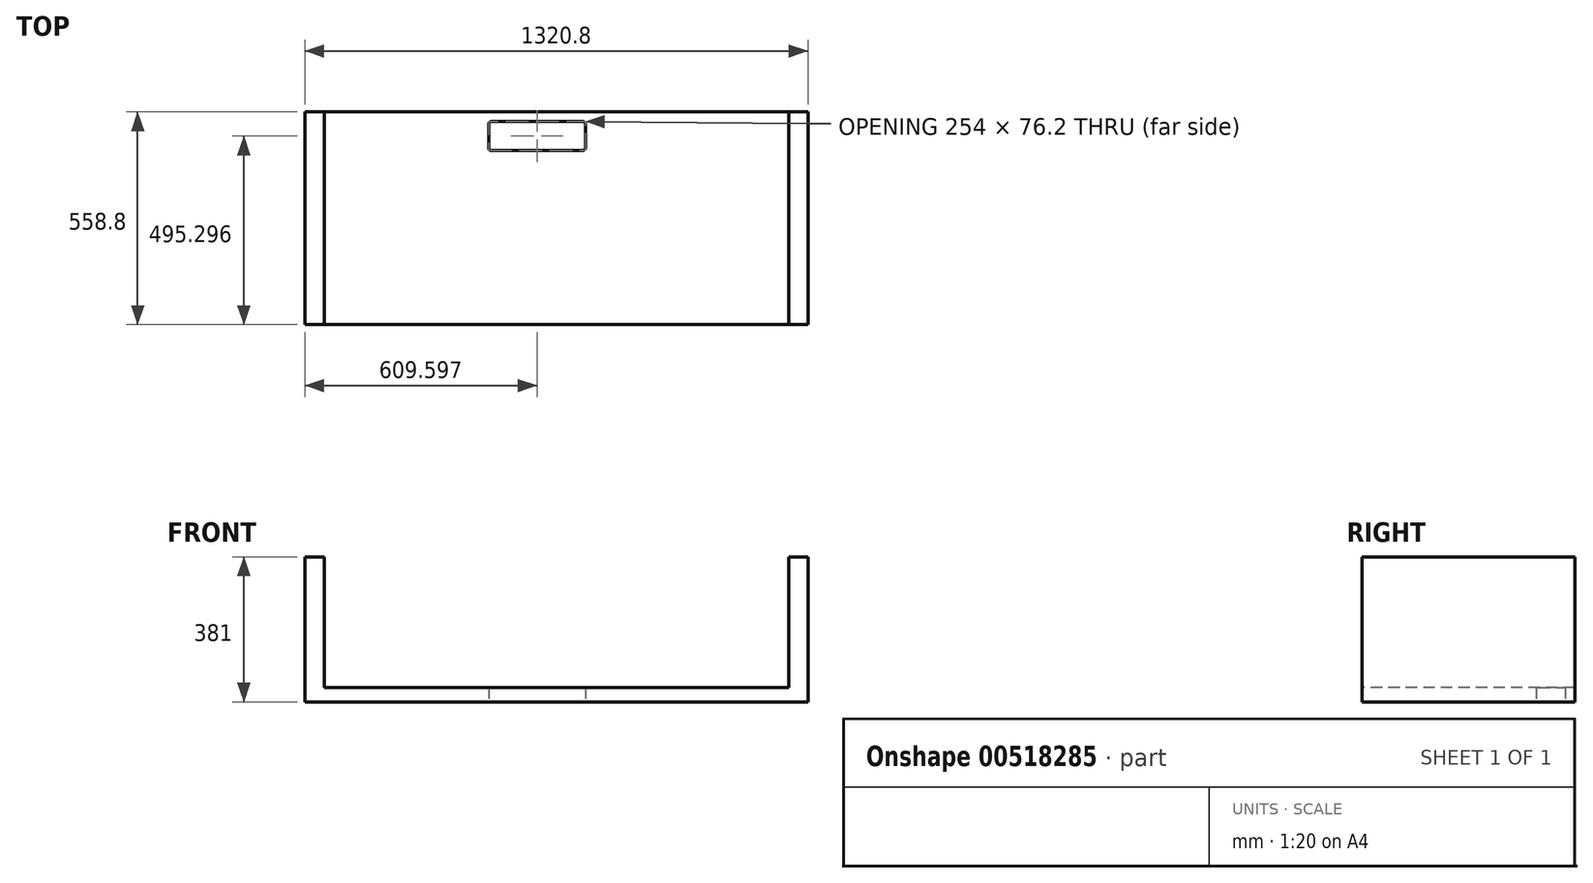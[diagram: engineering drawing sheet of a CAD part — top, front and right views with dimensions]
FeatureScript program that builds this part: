
annotation { "Feature Type Name" : "Feature", "Feature Type Description" : "" }
export const myFeature = defineFeature(function(context is Context, id is Id, definition is map)
    precondition{}
    {
        {
            var Q0;
            Q0=qCreatedBy(makeId("Top.planeOp"),FACE);
            var sketch = newSketch(context, id + "F0", { "sketchPlane" : qUnion([Q0])});
            skLineSegment(sketch, "E0.bottom", {"start": v(-660.38, -103.16) * mm, "end": v(660.42, -103.16) * mm});
            skLineSegment(sketch, "E0.top", {"start": v(-660.38, -661.96) * mm, "end": v(660.42, -661.96) * mm});
            skLineSegment(sketch, "E0.left", {"start": v(-660.38, -103.16) * mm, "end": v(-660.38, -661.96) * mm});
            skLineSegment(sketch, "E0.right", {"start": v(660.42, -103.16) * mm, "end": v(660.42, -661.96) * mm});
            skSolve(sketch);
        }
        {
            var Q0;
            Q0=makeQuery(id+"F0.imprint","IMPRINT",FACE,{"disambiguationData":[TD([[makeQuery(id+"F0.imprint","IMPRINT",EDGE,{"derivedFrom":sQuery(id+"F0.wireOp",EDGE,"E0.bottom")}),-1.0]])]});
            extrude(context, id + "F1", {"entities" : qUnion([Q0]), "depth" : 38.1 * mm, "offsetDistance" : 25.4 * mm});
        }
        {
            var Q0;
            Q0=makeQuery(id+"F1.opExtrude","CAP_FACE",FACE,{"disambiguationData":[OSD([sQuery(id+"F0.wireOp",EDGE,"E0.bottom"),sQuery(id+"F0.wireOp",EDGE,"E0.top"),sQuery(id+"F0.wireOp",EDGE,"E0.left"),sQuery(id+"F0.wireOp",EDGE,"E0.right")])],"isStart":false});
            var sketch = newSketch(context, id + "F2", { "sketchPlane" : qUnion([Q0])});
            skLineSegment(sketch, "E1.bottom", {"start": v(-660.38, -103.16) * mm, "end": v(-609.58, -103.16) * mm});
            skLineSegment(sketch, "E1.top", {"start": v(-660.38, -661.96) * mm, "end": v(-609.58, -661.96) * mm});
            skLineSegment(sketch, "E1.left", {"start": v(-660.38, -103.16) * mm, "end": v(-660.38, -661.96) * mm});
            skLineSegment(sketch, "E1.right", {"start": v(-609.58, -103.16) * mm, "end": v(-609.58, -661.96) * mm});
            skLineSegment(sketch, "E2.bottom", {"start": v(660.42, -103.16) * mm, "end": v(609.62, -103.16) * mm});
            skLineSegment(sketch, "E2.top", {"start": v(660.42, -661.96) * mm, "end": v(609.62, -661.96) * mm});
            skLineSegment(sketch, "E2.left", {"start": v(660.42, -103.16) * mm, "end": v(660.42, -661.96) * mm});
            skLineSegment(sketch, "E2.right", {"start": v(609.62, -103.16) * mm, "end": v(609.62, -661.96) * mm});
            skLineSegment(sketch, "E3.left", {"start": v(-609.58, -300.01) * mm, "end": v(-609.58, -319.06) * mm});
            skLineSegment(sketch, "E3.right", {"start": v(609.62, -300.01) * mm, "end": v(609.62, -319.06) * mm});
            skLineSegment(sketch, "E4.bottom", {"start": v(-177.78, -128.56) * mm, "end": v(76.22, -128.56) * mm});
            skLineSegment(sketch, "E4.top", {"start": v(-177.78, -204.76) * mm, "end": v(76.22, -204.76) * mm});
            skLineSegment(sketch, "E4.left", {"start": v(-177.78, -128.56) * mm, "end": v(-177.78, -204.76) * mm});
            skLineSegment(sketch, "E4.right", {"start": v(76.22, -128.56) * mm, "end": v(76.22, -204.76) * mm});
            skSolve(sketch);
        }
        {
            var Q0;
            Q0=makeQuery(id+"F2.imprint","IMPRINT",FACE,{"disambiguationData":[TD([[makeQuery(id+"F2.imprint","IMPRINT",EDGE,{"derivedFrom":sQuery(id+"F2.wireOp",EDGE,"E4.bottom")}),-1.0]])]});
            extrude(context, id + "F3", {"entities" : qUnion([Q0]), "operationType" : NewBodyOperationType.REMOVE, "endBound" : BoundingType.SYMMETRIC, "depth" : 666.5 * mm, "offsetDistance" : 25.4 * mm});
        }
        {
            var Q0;
            Q0=makeQuery(id+"F3.boolean.opBoolean","COPY",EDGE,{"derivedFrom":makeQuery(id+"F3.opExtrude","SWEPT_EDGE",EDGE,{"disambiguationData":[OSD([sQuery(id+"F2.wireOp",EDGE,"E4.bottom"),sQuery(id+"F2.wireOp",EDGE,"E4.left")])]})});
            var Q1;
            Q1=makeQuery(id+"F3.boolean.opBoolean","COPY",EDGE,{"derivedFrom":makeQuery(id+"F3.opExtrude","SWEPT_EDGE",EDGE,{"disambiguationData":[OSD([sQuery(id+"F2.wireOp",EDGE,"E4.top"),sQuery(id+"F2.wireOp",EDGE,"E4.left")])]})});
            var Q2;
            Q2=makeQuery(id+"F3.boolean.opBoolean","COPY",EDGE,{"derivedFrom":makeQuery(id+"F3.opExtrude","SWEPT_EDGE",EDGE,{"disambiguationData":[OSD([sQuery(id+"F2.wireOp",EDGE,"E4.bottom"),sQuery(id+"F2.wireOp",EDGE,"E4.right")])]})});
            var Q3;
            Q3=makeQuery(id+"F3.boolean.opBoolean","COPY",EDGE,{"derivedFrom":makeQuery(id+"F3.opExtrude","SWEPT_EDGE",EDGE,{"disambiguationData":[OSD([sQuery(id+"F2.wireOp",EDGE,"E4.top"),sQuery(id+"F2.wireOp",EDGE,"E4.right")])]})});
            fillet(context, id + "F4", {"entities" : qUnion([Q0, Q1, Q2, Q3]), "radius" : 6.35 * mm, "tangentPropagation" : true, "allowEdgeOverflow" : false});
        }
        {
            var Q0;
            {var subQ1=sQuery(id+"F2.wireOp",EDGE,"E1.bottom");Q0=makeQuery(id+"F2.imprint","IMPRINT",FACE,{"disambiguationData":[TD([[makeQuery(id+"F2.imprint","IMPRINT",EDGE,{"derivedFrom":subQ1}),-1.0]])]});}
            var Q1;
            {var subQ1=sQuery(id+"F2.wireOp",EDGE,"E2.bottom");Q1=makeQuery(id+"F2.imprint","IMPRINT",FACE,{"disambiguationData":[TD([[makeQuery(id+"F2.imprint","IMPRINT",EDGE,{"derivedFrom":subQ1}),-1.0]])]});}
            extrude(context, id + "F5", {"entities" : qUnion([Q0, Q1]), "operationType" : NewBodyOperationType.ADD, "depth" : 342.9 * mm, "offsetDistance" : 25.4 * mm});
        }
    });
